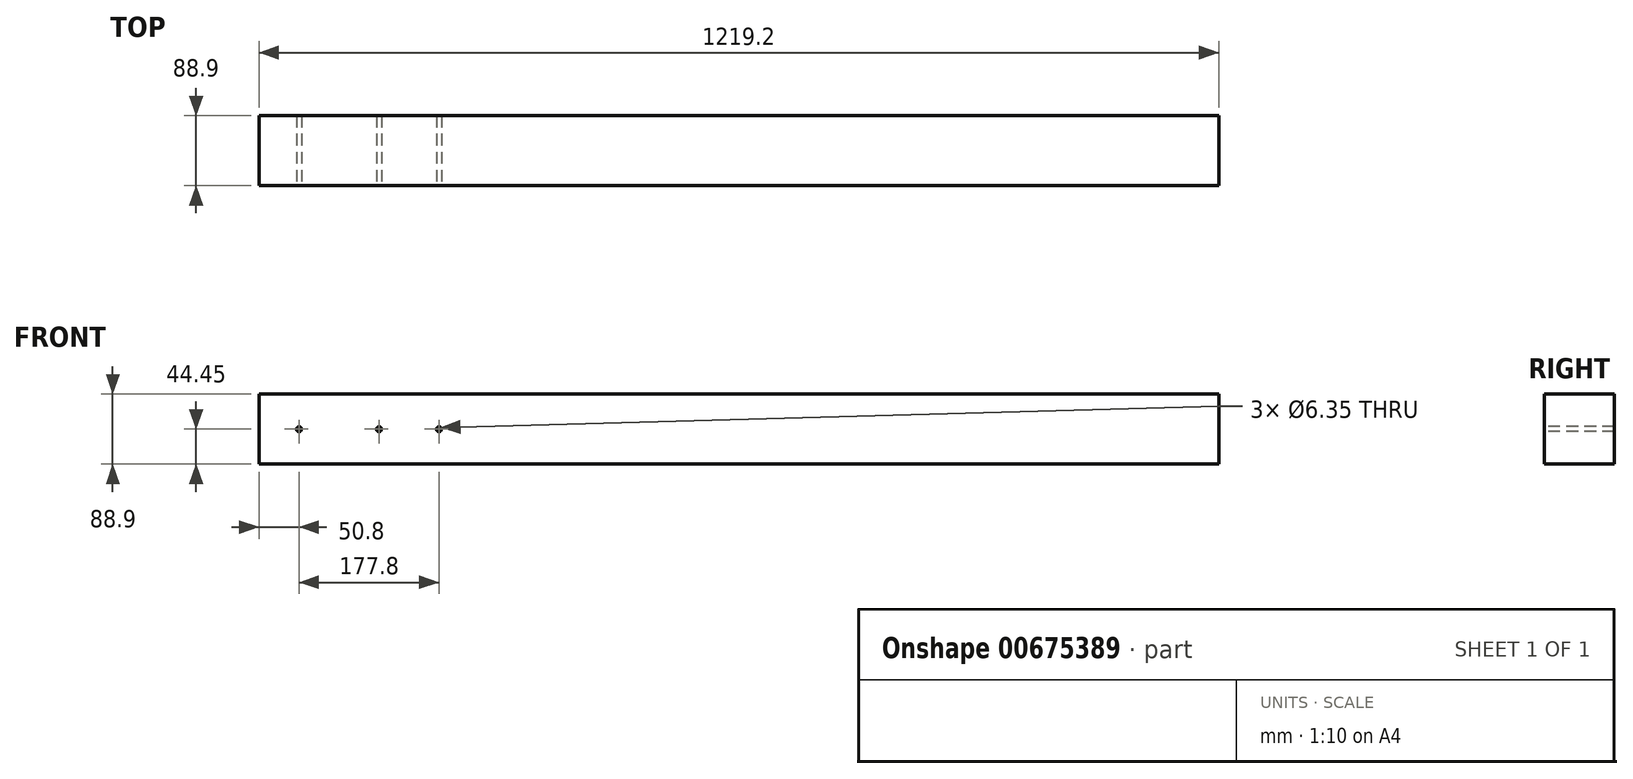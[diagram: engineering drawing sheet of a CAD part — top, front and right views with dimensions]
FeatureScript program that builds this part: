
annotation { "Feature Type Name" : "Feature", "Feature Type Description" : "" }
export const myFeature = defineFeature(function(context is Context, id is Id, definition is map)
    precondition{}
    {
        {
            var Q0;
            Q0=qCreatedBy(makeId("Top.planeOp"),FACE);
            var sketch = newSketch(context, id + "F0", { "sketchPlane" : qUnion([Q0])});
            skLineSegment(sketch, "E0.bottom", {"start": v(0, 0) * mm, "end": v(1219.2, 0) * mm});
            skLineSegment(sketch, "E1.top", {"start": v(0, -44.45) * mm, "end": v(1219.2, -44.45) * mm});
            skLineSegment(sketch, "E1.left", {"start": v(0, 0) * mm, "end": v(0, -44.45) * mm});
            skLineSegment(sketch, "E1.right", {"start": v(1219.2, 0) * mm, "end": v(1219.2, -44.45) * mm});
            skSolve(sketch);
        }
        {
            var Q0;
            Q0 = qSketchRegion(id + "F0", true);
            extrude(context, id + "F1", {"entities" : qUnion([Q0]), "depth" : 88.9 * mm, "offsetDistance" : 25.4 * mm});
        }
        {
            var Q0;
            Q0=qCreatedBy(makeId("Top.planeOp"),FACE);
            var sketch = newSketch(context, id + "F2", { "sketchPlane" : qUnion([Q0])});
            skLineSegment(sketch, "E2.bottom", {"start": v(0, 0) * mm, "end": v(1219.2, 0) * mm});
            skLineSegment(sketch, "E2.top", {"start": v(0, 44.45) * mm, "end": v(1219.2, 44.45) * mm});
            skLineSegment(sketch, "E2.left", {"start": v(0, 0) * mm, "end": v(0, 44.45) * mm});
            skLineSegment(sketch, "E2.right", {"start": v(1219.2, 0) * mm, "end": v(1219.2, 44.45) * mm});
            skSolve(sketch);
        }
        {
            var Q0;
            Q0 = qSketchRegion(id + "F2", true);
            extrude(context, id + "F3", {"entities" : qUnion([Q0]), "operationType" : NewBodyOperationType.ADD, "depth" : 88.9 * mm, "offsetDistance" : 25.4 * mm});
        }
        {
            var Q0;
            Q0=makeQuery(id+"F1.opExtrude","SWEPT_FACE",FACE,{"disambiguationData":[OSD([sQuery(id+"F0.wireOp",EDGE,"E1.top")])]});
            var sketch = newSketch(context, id + "F4", { "sketchPlane" : qUnion([Q0])});
            skCircle(sketch, "E3", {"center": v(50.8, 44.45) * mm, "radius": 3.18 * mm});
            skCircle(sketch, "E4", {"center": v(152.4, 44.45) * mm, "radius": 3.17 * mm});
            skCircle(sketch, "E5", {"center": v(228.6, 44.45) * mm, "radius": 3.17 * mm});
            skSolve(sketch);
        }
        {
            var Q0;
            Q0 = qSketchRegion(id + "F4", true);
            extrude(context, id + "F5", {"entities" : qUnion([Q0]), "operationType" : NewBodyOperationType.REMOVE, "endBound" : BoundingType.THROUGH_ALL, "oppositeDirection" : true, "depth" : 25.4 * mm, "offsetDistance" : 25.4 * mm});
        }
    });
